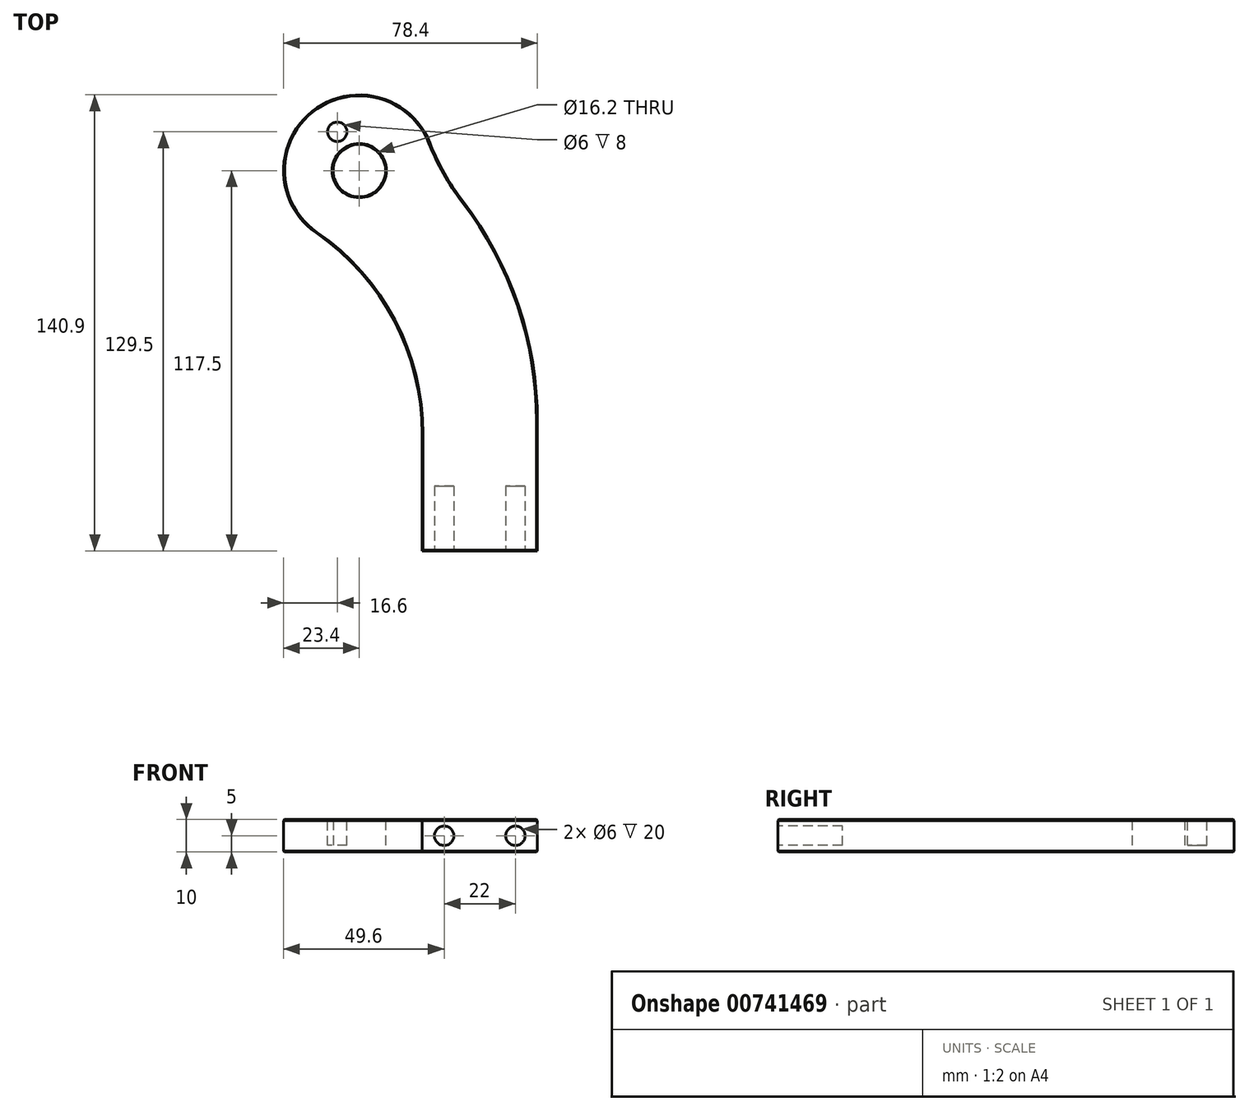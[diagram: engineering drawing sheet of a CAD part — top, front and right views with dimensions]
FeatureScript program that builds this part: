
annotation { "Feature Type Name" : "Feature", "Feature Type Description" : "" }
export const myFeature = defineFeature(function(context is Context, id is Id, definition is map)
    precondition{}
    {
        {
            var Q0;
            Q0=qCreatedBy(makeId("Top.planeOp"),FACE);
            var sketch = newSketch(context, id + "F0", { "sketchPlane" : qUnion([Q0])});
            skLineSegment(sketch, "E0", {"start": v(0, 0) * mm, "end": v(35.6, 0) * mm});
            skLineSegment(sketch, "E1", {"start": v(35.6, 0) * mm, "end": v(35.6, 40) * mm});
            skCircle(sketch, "E2", {"center": v(-19.4, 117.5) * mm, "radius": 8.1 * mm});
            skArc(sketch, "E3", {"start": v(2.36, 126.1) * mm, "mid": v(-33.97, 135.8) * mm, "end": v(-32.66, 98.22) * mm});
            skArc(sketch, "E4", {"start": v(2.36, 126.1) * mm, "mid": v(6.85, 116.7) * mm, "end": v(12.58, 108.01) * mm});
            skArc(sketch, "E5", {"start": v(35.6, 40) * mm, "mid": v(29.7, 75.9) * mm, "end": v(12.58, 108.01) * mm});
            skLineSegment(sketch, "E6", {"start": v(0, 0) * mm, "end": v(0, 36.1) * mm});
            skArc(sketch, "E7", {"start": v(0, 36.1) * mm, "mid": v(-8.66, 71.2) * mm, "end": v(-32.66, 98.22) * mm});
            skSolve(sketch);
        }
        {
            var Q0;
            Q0=makeQuery(id+"F0.imprint","IMPRINT",FACE,{"disambiguationData":[TD([[makeQuery(id+"F0.imprint","IMPRINT",EDGE,{"derivedFrom":sQuery(id+"F0.wireOp",EDGE,"E0")}),1.0]])]});
            extrude(context, id + "F1", {"entities" : qUnion([Q0]), "depth" : 10 * mm, "offsetDistance" : 25 * mm});
        }
        {
            var Q0;
            Q0=makeQuery(id+"F1.opExtrude","CAP_EDGE",EDGE,{"disambiguationData":[OSD([sQuery(id+"F0.wireOp",EDGE,"E0")])],"isStart":false});
            var Q1;
            Q1=makeQuery(id+"F1.opExtrude","CAP_EDGE",EDGE,{"disambiguationData":[OSD([sQuery(id+"F0.wireOp",EDGE,"E6")])],"isStart":false});
            var Q2;
            Q2=makeQuery(id+"F1.opExtrude","CAP_EDGE",EDGE,{"disambiguationData":[OSD([sQuery(id+"F0.wireOp",EDGE,"E2")])],"isStart":false});
            var Q3;
            Q3=makeQuery(id+"F1.opExtrude","CAP_EDGE",EDGE,{"disambiguationData":[OSD([sQuery(id+"F0.wireOp",EDGE,"E5")])],"isStart":true});
            var Q4;
            Q4=makeQuery(id+"F1.opExtrude","CAP_EDGE",EDGE,{"disambiguationData":[OSD([sQuery(id+"F0.wireOp",EDGE,"E2")])],"isStart":true});
            var Q5;
            Q5=makeQuery(id+"F1.opExtrude","CAP_EDGE",EDGE,{"disambiguationData":[OSD([sQuery(id+"F0.wireOp",EDGE,"E0")])],"isStart":true});
            chamfer(context, id + "F2", {"entities" : qUnion([Q0, Q1, Q2, Q3, Q4, Q5]), "width" : 0.3 * mm, "tangentPropagation" : true});
        }
        {
            var Q0;
            Q0=makeQuery(id+"F1.opExtrude","CAP_FACE",FACE,{"disambiguationData":[OSD([sQuery(id+"F0.wireOp",EDGE,"E0"),sQuery(id+"F0.wireOp",EDGE,"E1"),sQuery(id+"F0.wireOp",EDGE,"E2"),sQuery(id+"F0.wireOp",EDGE,"E3"),sQuery(id+"F0.wireOp",EDGE,"E4"),sQuery(id+"F0.wireOp",EDGE,"E5"),sQuery(id+"F0.wireOp",EDGE,"E6"),sQuery(id+"F0.wireOp",EDGE,"E7")])],"isStart":false});
            var sketch = newSketch(context, id + "F3", { "sketchPlane" : qUnion([Q0])});
            skCircle(sketch, "E8", {"center": v(-26.2, 129.5) * mm, "radius": 3 * mm});
            skCircle(sketch, "E9", {"center": v(-19.4, 117.5) * mm, "radius": 13.8 * mm, "construction": true});
            skSolve(sketch);
        }
        {
            var Q0;
            Q0=makeQuery(id+"F3.imprint","IMPRINT",FACE,{"disambiguationData":[TD([[makeQuery(id+"F3.imprint","IMPRINT",EDGE,{"derivedFrom":sQuery(id+"F3.wireOp",EDGE,"E8")}),1.0]])]});
            extrude(context, id + "F4", {"entities" : qUnion([Q0]), "operationType" : NewBodyOperationType.REMOVE, "oppositeDirection" : true, "depth" : 8 * mm, "offsetDistance" : 25 * mm});
        }
        {
            var Q0;
            Q0=makeQuery(id+"F1.opExtrude","SWEPT_FACE",FACE,{"disambiguationData":[OSD([sQuery(id+"F0.wireOp",EDGE,"E0")])]});
            var sketch = newSketch(context, id + "F5", { "sketchPlane" : qUnion([Q0])});
            skCircle(sketch, "E10", {"center": v(6.8, 5) * mm, "radius": 3 * mm});
            skCircle(sketch, "E11", {"center": v(28.8, 5) * mm, "radius": 3 * mm});
            skLineSegment(sketch, "E12", {"start": v(6.8, 5) * mm, "end": v(28.8, 5) * mm, "construction": true});
            skLineSegment(sketch, "E13", {"start": v(17.8, 5) * mm, "end": v(17.8, 14.81) * mm, "construction": true});
            skSolve(sketch);
        }
        {
            var Q0;
            Q0=makeQuery(id+"F5.imprint","IMPRINT",FACE,{"disambiguationData":[TD([[makeQuery(id+"F5.imprint","IMPRINT",EDGE,{"derivedFrom":sQuery(id+"F5.wireOp",EDGE,"E10")}),1.0]])]});
            var Q1;
            Q1=makeQuery(id+"F5.imprint","IMPRINT",FACE,{"disambiguationData":[TD([[makeQuery(id+"F5.imprint","IMPRINT",EDGE,{"derivedFrom":sQuery(id+"F5.wireOp",EDGE,"E11")}),1.0]])]});
            extrude(context, id + "F6", {"entities" : qUnion([Q0, Q1]), "operationType" : NewBodyOperationType.REMOVE, "oppositeDirection" : true, "depth" : 20 * mm, "offsetDistance" : 25 * mm});
        }
    });
